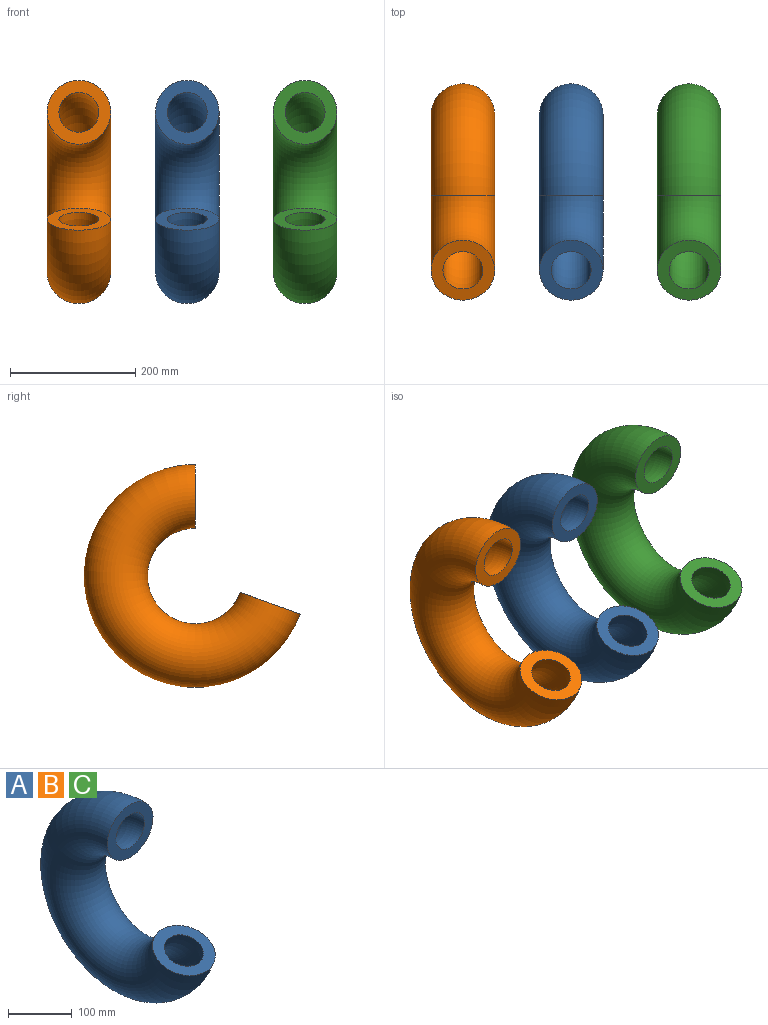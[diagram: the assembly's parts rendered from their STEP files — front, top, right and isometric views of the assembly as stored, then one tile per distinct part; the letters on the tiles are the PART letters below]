
ASSEMBLY  parts=3 mates=2
PART A: 4 faces, bbox 101.6x373.3x384.9 mm
  f0: torus R=127mm, axis (1,0,0), area 110546.4mm2, adj f2,f3
  f1: torus R=127mm, axis (1,0,0), area 176874.3mm2, adj f2,f3
  f2: plane 101.6x95.47mm, normal (0,-0.34,0.94), area 4940.4mm2, adj f0,f1
  f3: plane 101.6x101.6mm, normal (0,-1,0), area 4940.4mm2, adj f0,f1
PART B: same geometry as A
PART C: same geometry as A
PLACE A t=(172.72,0,0)mm
PLACE B at identity
PLACE C t=(360.68,0,0)mm
MATE planar B.f3 <-> C.f3  axis (0,-1,0) through (0,0,0)mm
MATE planar B.f3 <-> A.f3  axis (0,-1,0) through (0,0,0)mm
